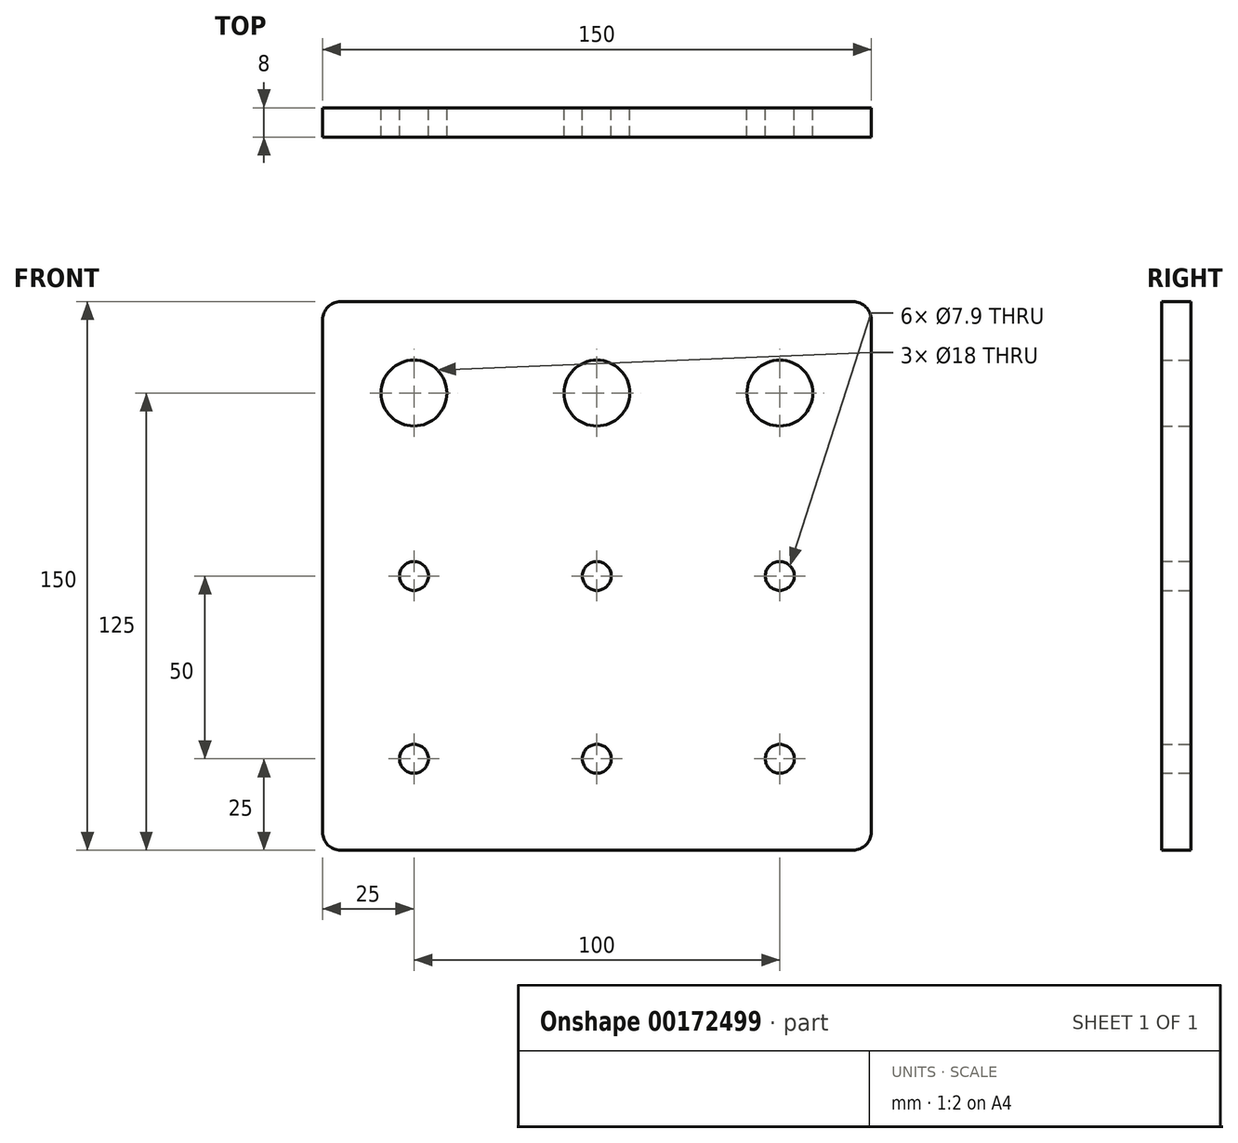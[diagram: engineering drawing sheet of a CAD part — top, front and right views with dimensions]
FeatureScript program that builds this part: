
annotation { "Feature Type Name" : "Feature", "Feature Type Description" : "" }
export const myFeature = defineFeature(function(context is Context, id is Id, definition is map)
    precondition{}
    {
        {
            var Q0;
            Q0=qCreatedBy(makeId("Front.planeOp"),FACE);
            var sketch = newSketch(context, id + "F0", { "sketchPlane" : qUnion([Q0])});
            skLineSegment(sketch, "E0", {"start": v(0, 0) * mm, "end": v(0, 100) * mm, "construction": true});
            skLineSegment(sketch, "E1.bottom", {"start": v(75, -75) * mm, "end": v(-75, -75) * mm});
            skLineSegment(sketch, "E1.top", {"start": v(75, 75) * mm, "end": v(-75, 75) * mm});
            skLineSegment(sketch, "E1.left", {"start": v(75, -75) * mm, "end": v(75, 75) * mm});
            skLineSegment(sketch, "E1.right", {"start": v(-75, -75) * mm, "end": v(-75, 75) * mm});
            skPoint(sketch, "E1.middle", {"position": v(0, 0) * mm});
            skCircle(sketch, "E2", {"center": v(0, 50) * mm, "radius": 9 * mm});
            skCircle(sketch, "E3", {"center": v(0, 0) * mm, "radius": 3.95 * mm});
            skLineSegment(sketch, "E4", {"start": v(0, -75) * mm, "end": v(0, -25) * mm, "construction": true});
            skCircle(sketch, "E5", {"center": v(0, -50) * mm, "radius": 3.95 * mm});
            skLineSegment(sketch, "E6", {"start": v(0, 0) * mm, "end": v(-75, 0) * mm, "construction": true});
            skLineSegment(sketch, "E7", {"start": v(-25, 0) * mm, "end": v(-25, 18.93) * mm, "construction": true});
            skLineSegment(sketch, "E8.MirrorCS", {"start": v(25, 0) * mm, "end": v(25, 18.93) * mm, "construction": true});
            skCircle(sketch, "E9.MirrorC", {"center": v(-50, 50) * mm, "radius": 9 * mm});
            skCircle(sketch, "E10.MirrorC", {"center": v(-50, 0) * mm, "radius": 3.95 * mm});
            skCircle(sketch, "E11.MirrorC", {"center": v(-50, -50) * mm, "radius": 3.95 * mm});
            skCircle(sketch, "E12.MirrorC", {"center": v(50, 50) * mm, "radius": 9 * mm});
            skCircle(sketch, "E13.MirrorC", {"center": v(50, 0) * mm, "radius": 3.95 * mm});
            skCircle(sketch, "E14.MirrorC", {"center": v(50, -50) * mm, "radius": 3.95 * mm});
            skSolve(sketch);
        }
        {
            var Q0;
            Q0 = qSketchRegion(id + "F0", true);
            extrude(context, id + "F1", {"entities" : qUnion([Q0]), "depth" : 8 * mm});
        }
        {
            var Q0;
            Q0=makeQuery(id+"F1.opExtrude","SWEPT_EDGE",EDGE,{"disambiguationData":[OSD([sQuery(id+"F0.wireOp",EDGE,"E1.top"),sQuery(id+"F0.wireOp",EDGE,"E1.left")])]});
            fillet(context, id + "F2", {"entities" : qUnion([Q0]), "radius" : 5 * mm, "tangentPropagation" : true, "allowEdgeOverflow" : false});
        }
        {
            var Q0;
            Q0=makeQuery(id+"F1.opExtrude","SWEPT_EDGE",EDGE,{"disambiguationData":[OSD([sQuery(id+"F0.wireOp",EDGE,"E1.bottom"),sQuery(id+"F0.wireOp",EDGE,"E1.left")])]});
            fillet(context, id + "F3", {"entities" : qUnion([Q0]), "radius" : 5 * mm, "tangentPropagation" : true, "allowEdgeOverflow" : false});
        }
        {
            var Q0;
            Q0=makeQuery(id+"F1.opExtrude","SWEPT_EDGE",EDGE,{"disambiguationData":[OSD([sQuery(id+"F0.wireOp",EDGE,"E1.bottom"),sQuery(id+"F0.wireOp",EDGE,"E1.right")])]});
            fillet(context, id + "F4", {"entities" : qUnion([Q0]), "radius" : 5 * mm, "tangentPropagation" : true, "allowEdgeOverflow" : false});
        }
        {
            var Q0;
            Q0=makeQuery(id+"F1.opExtrude","SWEPT_EDGE",EDGE,{"disambiguationData":[OSD([sQuery(id+"F0.wireOp",EDGE,"E1.top"),sQuery(id+"F0.wireOp",EDGE,"E1.right")])]});
            fillet(context, id + "F5", {"entities" : qUnion([Q0]), "radius" : 5 * mm, "tangentPropagation" : true, "allowEdgeOverflow" : false});
        }
    });
